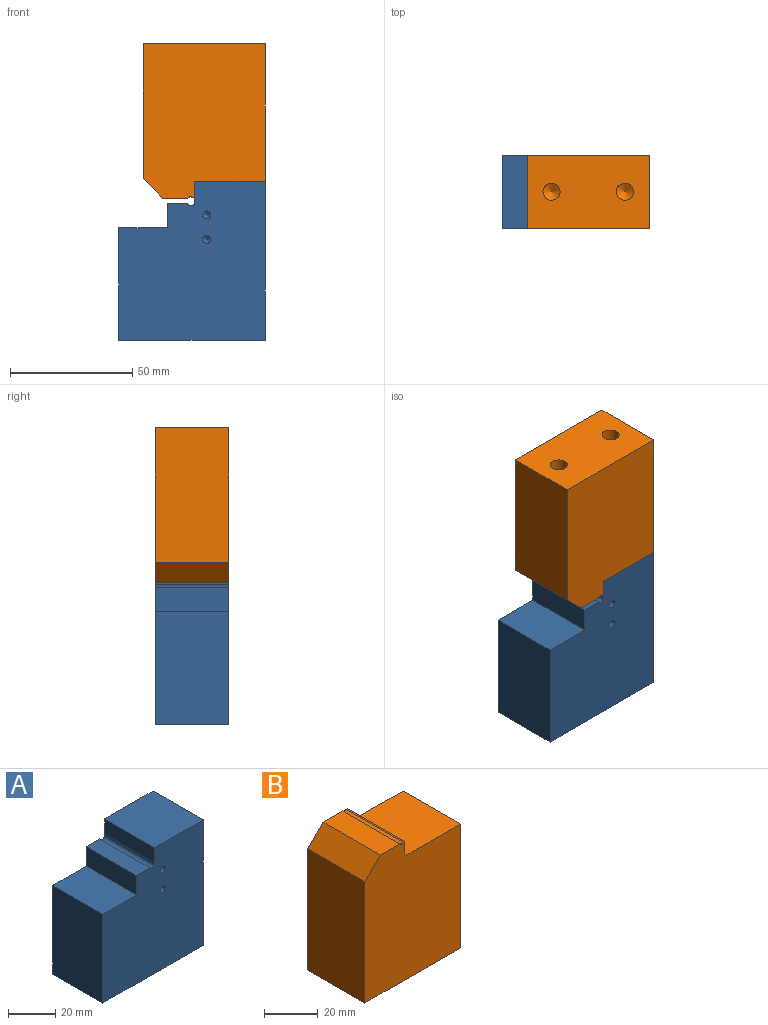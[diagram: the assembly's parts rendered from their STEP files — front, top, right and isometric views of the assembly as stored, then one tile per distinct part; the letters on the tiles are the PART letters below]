
ASSEMBLY  parts=2 mates=1
PART A: 23 faces, bbox 60x30x65 mm
  f0: plane 30x8.19mm, normal (0,0,1), area 245.6mm2, adj f5,f6,f8,f10
  f1: plane 30x29mm, normal (0,0,1), area 870mm2, adj f3,f5,f6,f9
  f2: plane 60x30mm, normal (0,0,-1), area 1727.4mm2, adj f3,f4,f5,f6,f20,f22
  f3: plane 65x30mm, normal (1,0,0), area 1950mm2, adj f1,f2,f5,f6
  f4: plane 46.05x30mm, normal (-1,0,0), area 1381.5mm2, adj f2,f5,f6,f7
  f5: plane 65x60mm, normal (0,-1,0), area 3403.3mm2, adj f0,f1,f2,f3,f4,f7,f8,f9
  f6: plane 65x60mm, normal (0,1,0), area 3403.3mm2, adj f0,f1,f2,f3,f4,f7,f8,f9
  f7: plane 30x20mm, normal (0,0,1), area 600mm2, adj f4,f5,f6,f8
  f8: plane 30x10mm, normal (-1,0,0), area 300mm2, adj f0,f5,f6,f7
  f9: plane 30x7.91mm, normal (-1,0,0), area 237.3mm2, adj f1,f5,f6,f10
  f10: cylinder r=1.5mm len=30mm, axis (0,-1,0), area 142.6mm2, adj f0,f5,f6,f9
  f11: cone r=0mm half-angle=59deg, axis (0,-1,0), area 10mm2, adj f12
  f12: cylinder r=1.65mm len=12mm, axis (0,-1,0), area 124.4mm2, adj f5,f11
  f13: cone r=0mm half-angle=59deg, axis (0,-1,0), area 10mm2, adj f14
  f14: cylinder r=1.65mm len=12mm, axis (0,-1,0), area 124.4mm2, adj f5,f13
  f15: cone r=0mm half-angle=59deg, axis (0,1,0), area 10mm2, adj f16
  f16: cylinder r=1.65mm len=12mm, axis (0,1,0), area 124.4mm2, adj f6,f15
  f17: cone r=0mm half-angle=59deg, axis (0,1,0), area 10mm2, adj f18
  f18: cylinder r=1.65mm len=12mm, axis (0,1,0), area 124.4mm2, adj f6,f17
  f19: cone r=0mm half-angle=59deg, axis (0,0,-1), area 42.4mm2, adj f20
  f20: cylinder r=3.4mm len=20mm, axis (0,0,-1), area 427.3mm2, adj f2,f19
  f21: cone r=0mm half-angle=59deg, axis (0,0,-1), area 42.4mm2, adj f22
  f22: cylinder r=3.4mm len=20mm, axis (0,0,-1), area 427.3mm2, adj f2,f21
PART B: 15 faces, bbox 50x30x63.2 mm
  f0: cylinder r=1.5mm len=30mm, axis (0,-1,0), area 61.4mm2, adj f1,f2,f5,f10
  f1: plane 63.15x50mm, normal (0,-1,0), area 2925.9mm2, adj f0,f3,f4,f5,f6,f7,f8,f9
  f2: plane 63.15x50mm, normal (0,1,0), area 2925.9mm2, adj f0,f3,f4,f5,f6,f7,f8,f9
  f3: plane 56.3x30mm, normal (1,0,0), area 1689mm2, adj f1,f2,f4,f8
  f4: plane 50x30mm, normal (0,0,-1), area 1423mm2, adj f1,f2,f3,f6,f12,f14
  f5: plane 30x10.28mm, normal (0,0,1), area 308.5mm2, adj f0,f1,f2,f9
  f6: plane 55.15x30mm, normal (-1,0,0), area 1654.5mm2, adj f1,f2,f4,f9
  f7: plane 30x6.55mm, normal (1,0,0), area 196.5mm2, adj f1,f2,f8,f10
  f8: plane 30x29mm, normal (0,0,1), area 870mm2, adj f1,f2,f3,f7
  f9: plane 30x8mm, normal (-0.71,0,0.71), area 339.4mm2, adj f1,f2,f5,f6
  f10: plane 30x0.85mm, normal (0,0,1), area 25.6mm2, adj f0,f1,f2,f7
  f11: cone r=0mm half-angle=59deg, axis (0,0,-1), area 44.9mm2, adj f12
  f12: cylinder r=3.5mm len=15mm, axis (0,0,-1), area 329.9mm2, adj f4,f11
  f13: cone r=0mm half-angle=59deg, axis (0,0,-1), area 44.9mm2, adj f14
  f14: cylinder r=3.5mm len=15mm, axis (0,0,-1), area 329.9mm2, adj f4,f13
PLACE A t=(-7.51,14.8,-10.97)mm
PLACE B rot(axis=(1,0,0),180deg) t=(2.49,-15.2,67.23)mm
MATE fastened B.f8 <-> A.f1  axis (0,0,-1) through (15.18,-0.2,32.48)mm
